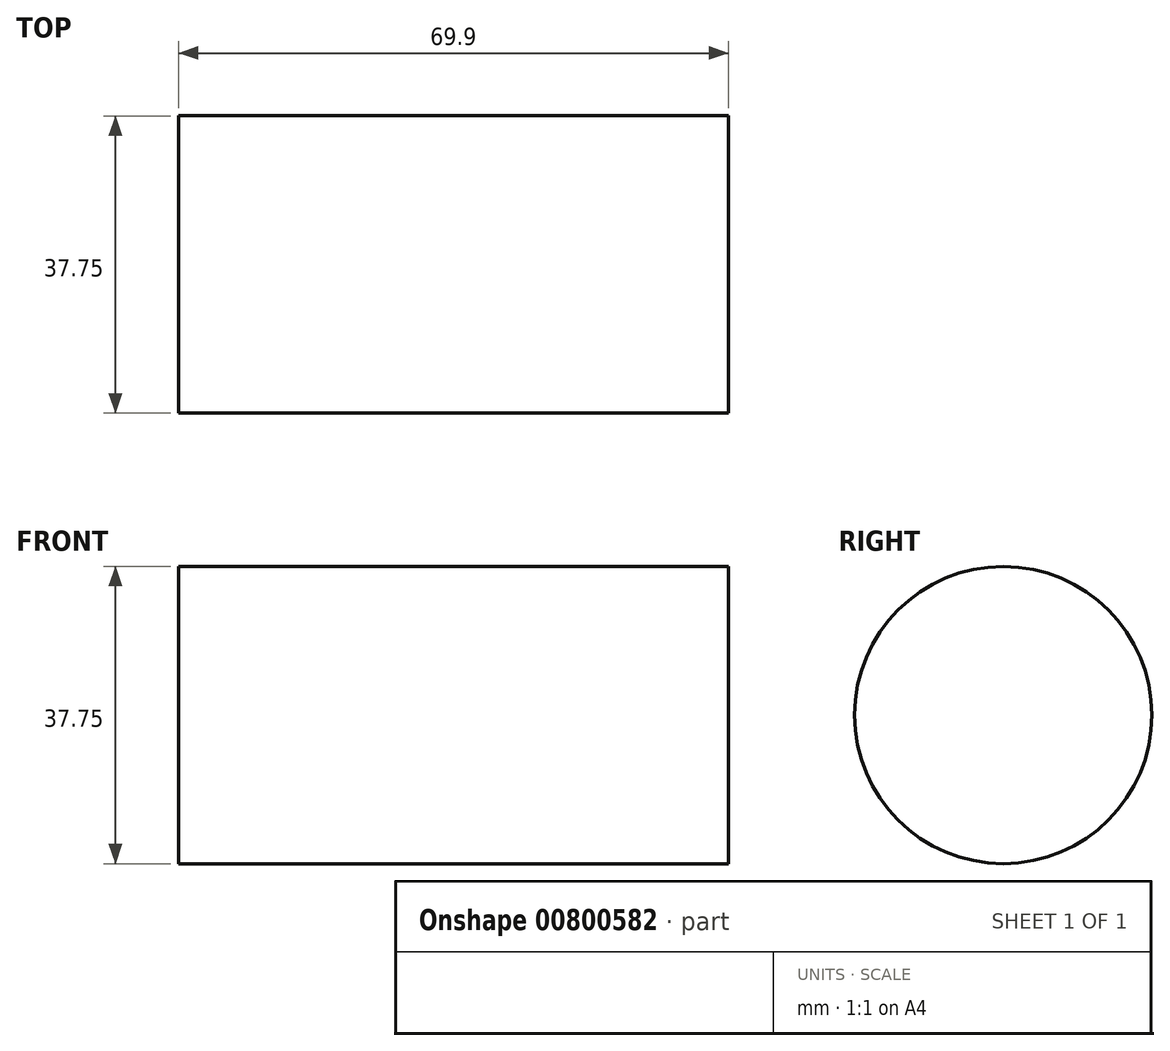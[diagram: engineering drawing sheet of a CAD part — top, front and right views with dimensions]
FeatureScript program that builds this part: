
annotation { "Feature Type Name" : "Feature", "Feature Type Description" : "" }
export const myFeature = defineFeature(function(context is Context, id is Id, definition is map)
    precondition{}
    {
        {
            var Q0;
            Q0=qCreatedBy(makeId("Right.planeOp"),FACE);
            var sketch = newSketch(context, id + "F0", { "sketchPlane" : qUnion([Q0])});
            skCircle(sketch, "E0", {"center": v(-30.06, 24.44) * mm, "radius": 18.87 * mm});
            skSolve(sketch);
        }
        {
            var Q0;
            Q0=makeQuery(id+"F0.imprint","IMPRINT",FACE,{"disambiguationData":[TD([[makeQuery(id+"F0.imprint","IMPRINT",EDGE,{"derivedFrom":sQuery(id+"F0.wireOp",EDGE,"E0")}),1.0]])]});
            extrude(context, id + "F1", {"entities" : qUnion([Q0]), "oppositeDirection" : true, "depth" : 69.9 * mm, "offsetDistance" : 25 * mm});
        }
    });
